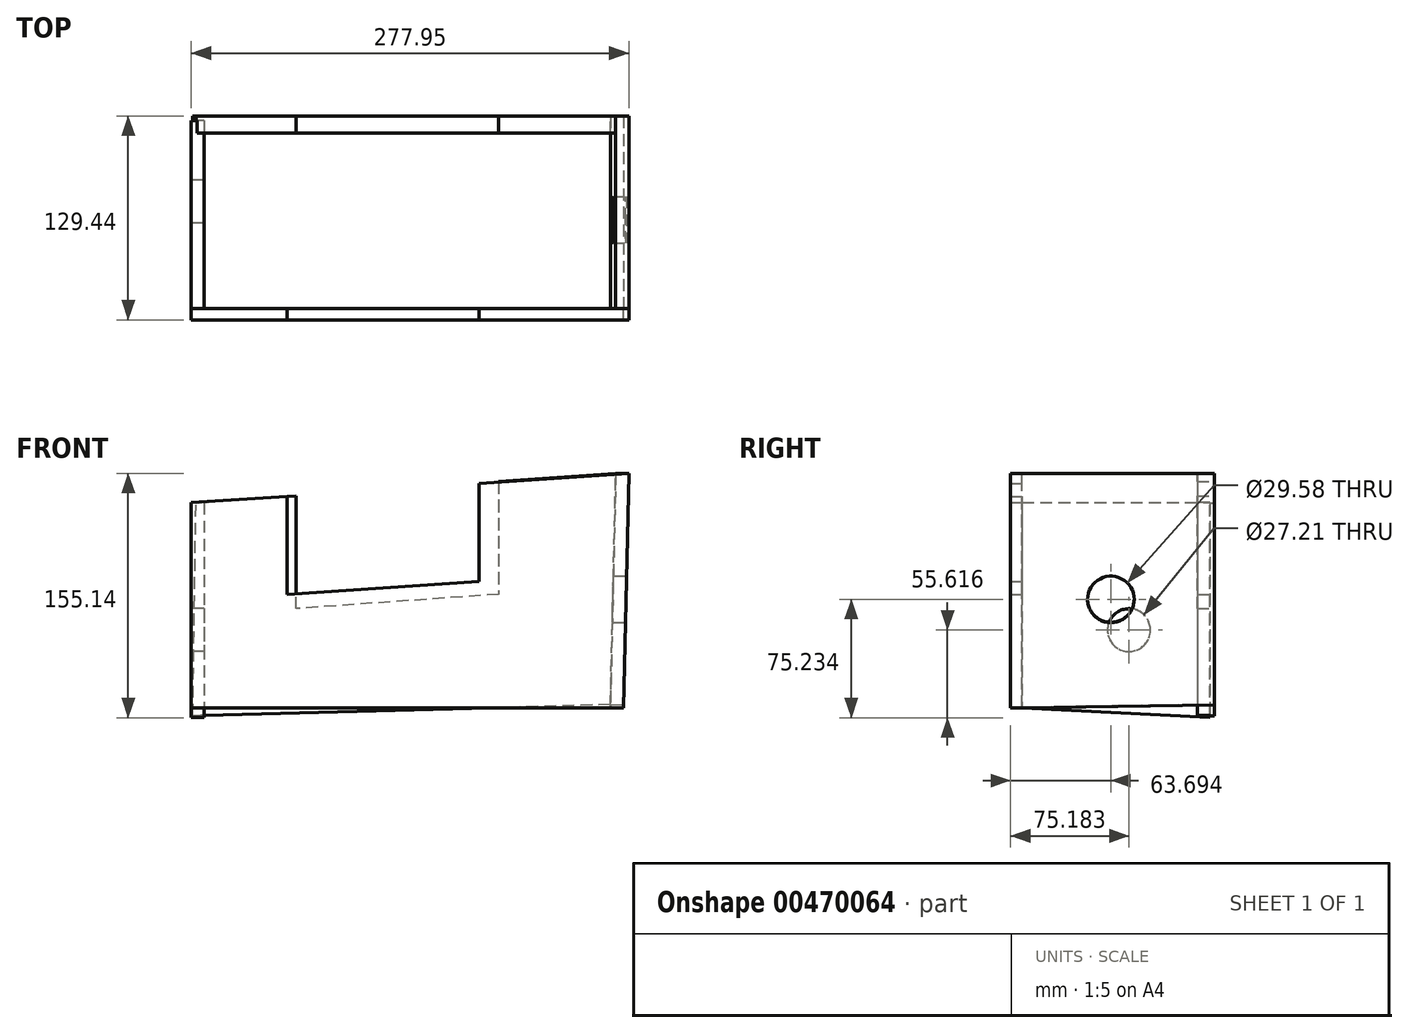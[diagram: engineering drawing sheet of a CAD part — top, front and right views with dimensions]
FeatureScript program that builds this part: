
annotation { "Feature Type Name" : "Feature", "Feature Type Description" : "" }
export const myFeature = defineFeature(function(context is Context, id is Id, definition is map)
    precondition{}
    {
        {
            var Q0;
            Q0=qCreatedBy(makeId("Front.planeOp"),FACE);
            var sketch = newSketch(context, id + "F0", { "sketchPlane" : qUnion([Q0])});
            skLineSegment(sketch, "E0", {"start": v(-137.27, 58.22) * mm, "end": v(-137.27, -72.03) * mm});
            skLineSegment(sketch, "E1", {"start": v(-137.27, -72.03) * mm, "end": v(137.27, -72.03) * mm});
            skLineSegment(sketch, "E2", {"start": v(137.27, -72.03) * mm, "end": v(140.68, 76.63) * mm});
            skLineSegment(sketch, "E3", {"start": v(-76.43, 62.25) * mm, "end": v(-76.43, 0) * mm});
            skLineSegment(sketch, "E4", {"start": v(-76.43, 0) * mm, "end": v(45.38, 8.07) * mm});
            skLineSegment(sketch, "E5", {"start": v(45.38, 8.07) * mm, "end": v(45.38, 70.32) * mm});
            skLineSegment(sketch, "E6.trimOffspring", {"start": v(-76.43, 62.25) * mm, "end": v(-137.27, 58.22) * mm});
            skLineSegment(sketch, "E7", {"start": v(45.38, 70.32) * mm, "end": v(140.68, 76.63) * mm});
            skSolve(sketch);
        }
        {
            var Q0;
            Q0=makeQuery(id+"F0.imprint","IMPRINT",FACE,{"disambiguationData":[TD([[makeQuery(id+"F0.imprint","IMPRINT",EDGE,{"derivedFrom":sQuery(id+"F0.wireOp",EDGE,"E0")}),1.0]])]});
            extrude(context, id + "F1", {"entities" : qUnion([Q0]), "depth" : 7.37 * mm});
        }
        {
            var Q0;
            Q0=makeQuery(id+"F1.opExtrude","SWEPT_FACE",FACE,{"disambiguationData":[OSD([sQuery(id+"F0.wireOp",EDGE,"E2")])]});
            var sketch = newSketch(context, id + "F2", { "sketchPlane" : qUnion([Q0])});
            skLineSegment(sketch, "E8", {"start": v(0, 79.83) * mm, "end": v(122.07, 79.83) * mm});
            skLineSegment(sketch, "E9", {"start": v(122.07, 79.83) * mm, "end": v(122.07, -67.03) * mm});
            skLineSegment(sketch, "E10", {"start": v(122.07, -67.03) * mm, "end": v(0, -68.87) * mm});
            skCircle(sketch, "E11", {"center": v(56.32, 0) * mm, "radius": 14.79 * mm});
            skSolve(sketch);
        }
        {
            var Q0;
            Q0=makeQuery(id+"F1.opExtrude","SWEPT_FACE",FACE,{"disambiguationData":[OSD([sQuery(id+"F0.wireOp",EDGE,"E0")])]});
            var sketch = newSketch(context, id + "F3", { "sketchPlane" : qUnion([Q0])});
            skLineSegment(sketch, "E12", {"start": v(0, 58.22) * mm, "end": v(-119.27, 58.22) * mm});
            skLineSegment(sketch, "E13", {"start": v(-119.27, 58.22) * mm, "end": v(-119.27, -78.32) * mm});
            skLineSegment(sketch, "E14", {"start": v(-119.27, -78.32) * mm, "end": v(0, -72.03) * mm});
            skCircle(sketch, "E15", {"center": v(-67.81, -22.7) * mm, "radius": 13.6 * mm});
            skSolve(sketch);
        }
        {
            var Q0;
            Q0=makeQuery(id+"F2.imprint","IMPRINT",FACE,{"disambiguationData":[TD([[makeQuery(id+"F2.imprint","IMPRINT",EDGE,{"derivedFrom":sQuery(id+"F2.wireOp",EDGE,"E8")}),-1.0]])]});
            extrude(context, id + "F4", {"entities" : qUnion([Q0]), "operationType" : NewBodyOperationType.ADD, "oppositeDirection" : true, "depth" : 8.38 * mm});
        }
        {
            var Q0;
            Q0=makeQuery(id+"F3.imprint","IMPRINT",FACE,{"disambiguationData":[TD([[makeQuery(id+"F3.imprint","IMPRINT",EDGE,{"derivedFrom":sQuery(id+"F3.wireOp",EDGE,"E12")}),1.0]])]});
            extrude(context, id + "F5", {"entities" : qUnion([Q0]), "operationType" : NewBodyOperationType.ADD, "oppositeDirection" : true, "depth" : 8.13 * mm});
        }
        {
            var Q0;
            Q0=makeQuery(id+"F4.opExtrude","SWEPT_FACE",FACE,{"disambiguationData":[OSD([sQuery(id+"F2.wireOp",EDGE,"E9")])]});
            var sketch = newSketch(context, id + "F6", { "sketchPlane" : qUnion([Q0])});
            skLineSegment(sketch, "E16", {"start": v(-128.93, -70) * mm, "end": v(136.4, -77.08) * mm});
            skLineSegment(sketch, "E17", {"start": v(136.4, -77.08) * mm, "end": v(134.34, 58.16) * mm});
            skLineSegment(sketch, "E18", {"start": v(134.34, 58.16) * mm, "end": v(70.82, 62.6) * mm});
            skLineSegment(sketch, "E19", {"start": v(-57.94, 71.62) * mm, "end": v(-57.94, 0) * mm});
            skLineSegment(sketch, "E20", {"start": v(-57.94, 0) * mm, "end": v(70.82, -9.01) * mm});
            skLineSegment(sketch, "E21", {"start": v(70.82, -9.01) * mm, "end": v(70.82, 62.6) * mm});
            skLineSegment(sketch, "E22.trimOffspring", {"start": v(-57.94, 71.62) * mm, "end": v(-132.3, 76.82) * mm});
            skSolve(sketch);
        }
        {
            var Q0;
            Q0=makeQuery(id+"F6.imprint","IMPRINT",FACE,{"disambiguationData":[TD([[makeQuery(id+"F6.imprint","IMPRINT",EDGE,{"derivedFrom":sQuery(id+"F6.wireOp",EDGE,"E16")}),1.0]])]});
            extrude(context, id + "F7", {"entities" : qUnion([Q0]), "operationType" : NewBodyOperationType.ADD, "oppositeDirection" : true, "depth" : 10.92 * mm});
        }
    });
